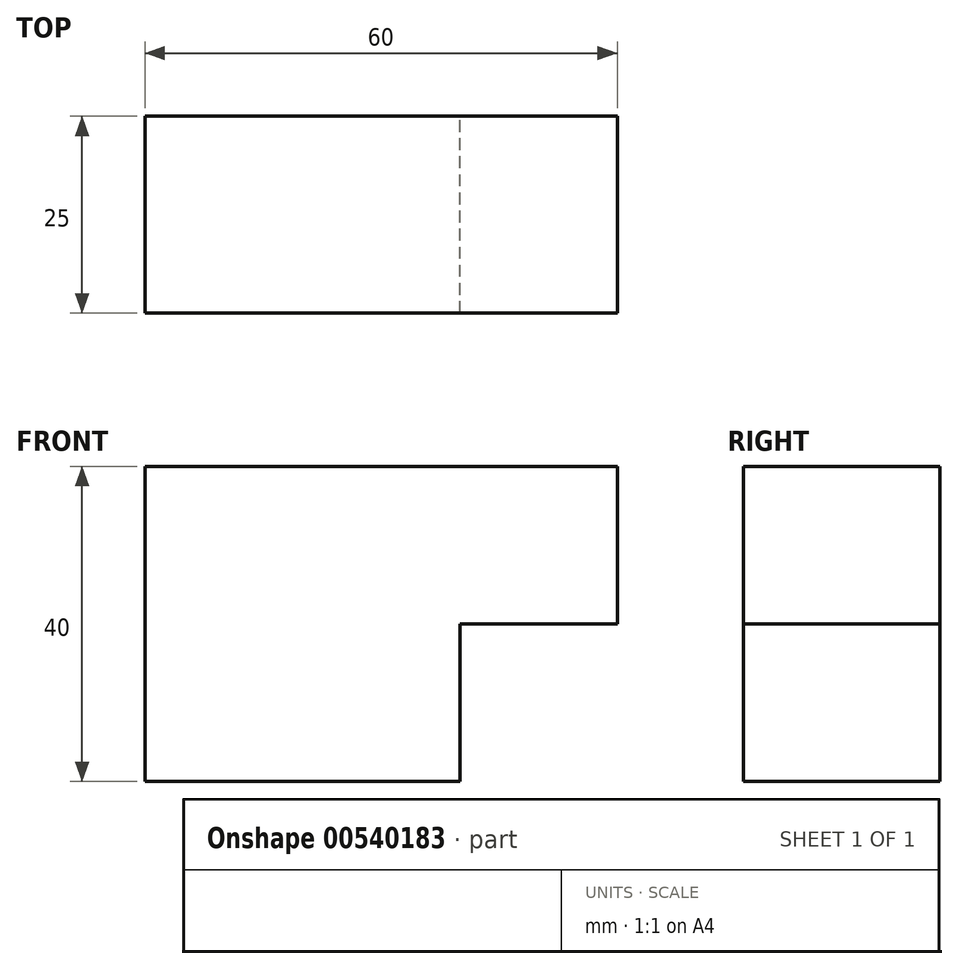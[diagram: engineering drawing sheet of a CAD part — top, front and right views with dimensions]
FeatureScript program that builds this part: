
annotation { "Feature Type Name" : "Feature", "Feature Type Description" : "" }
export const myFeature = defineFeature(function(context is Context, id is Id, definition is map)
    precondition{}
    {
        {
            var Q0;
            Q0=qCreatedBy(makeId("Front.planeOp"),FACE);
            var sketch = newSketch(context, id + "F0", { "sketchPlane" : qUnion([Q0])});
            skLineSegment(sketch, "E0", {"start": v(-42.94, 29.77) * mm, "end": v(17.06, 29.77) * mm});
            skLineSegment(sketch, "E1", {"start": v(17.06, 29.77) * mm, "end": v(17.06, 9.77) * mm});
            skLineSegment(sketch, "E2", {"start": v(17.06, 9.77) * mm, "end": v(-2.94, 9.77) * mm});
            skLineSegment(sketch, "E3", {"start": v(-2.94, 9.77) * mm, "end": v(-2.94, -10.23) * mm});
            skLineSegment(sketch, "E4", {"start": v(-2.94, -10.23) * mm, "end": v(-42.94, -10.23) * mm});
            skLineSegment(sketch, "E5", {"start": v(-42.94, -10.23) * mm, "end": v(-42.94, 29.77) * mm});
            skSolve(sketch);
        }
        {
            var Q0;
            Q0=makeQuery(id+"F0.imprint","IMPRINT",FACE,{"disambiguationData":[TD([[makeQuery(id+"F0.imprint","IMPRINT",EDGE,{"derivedFrom":sQuery(id+"F0.wireOp",EDGE,"E0")}),-1.0]])]});
            extrude(context, id + "F1", {"entities" : qUnion([Q0]), "depth" : 25 * mm, "offsetDistance" : 25 * mm});
        }
    });
